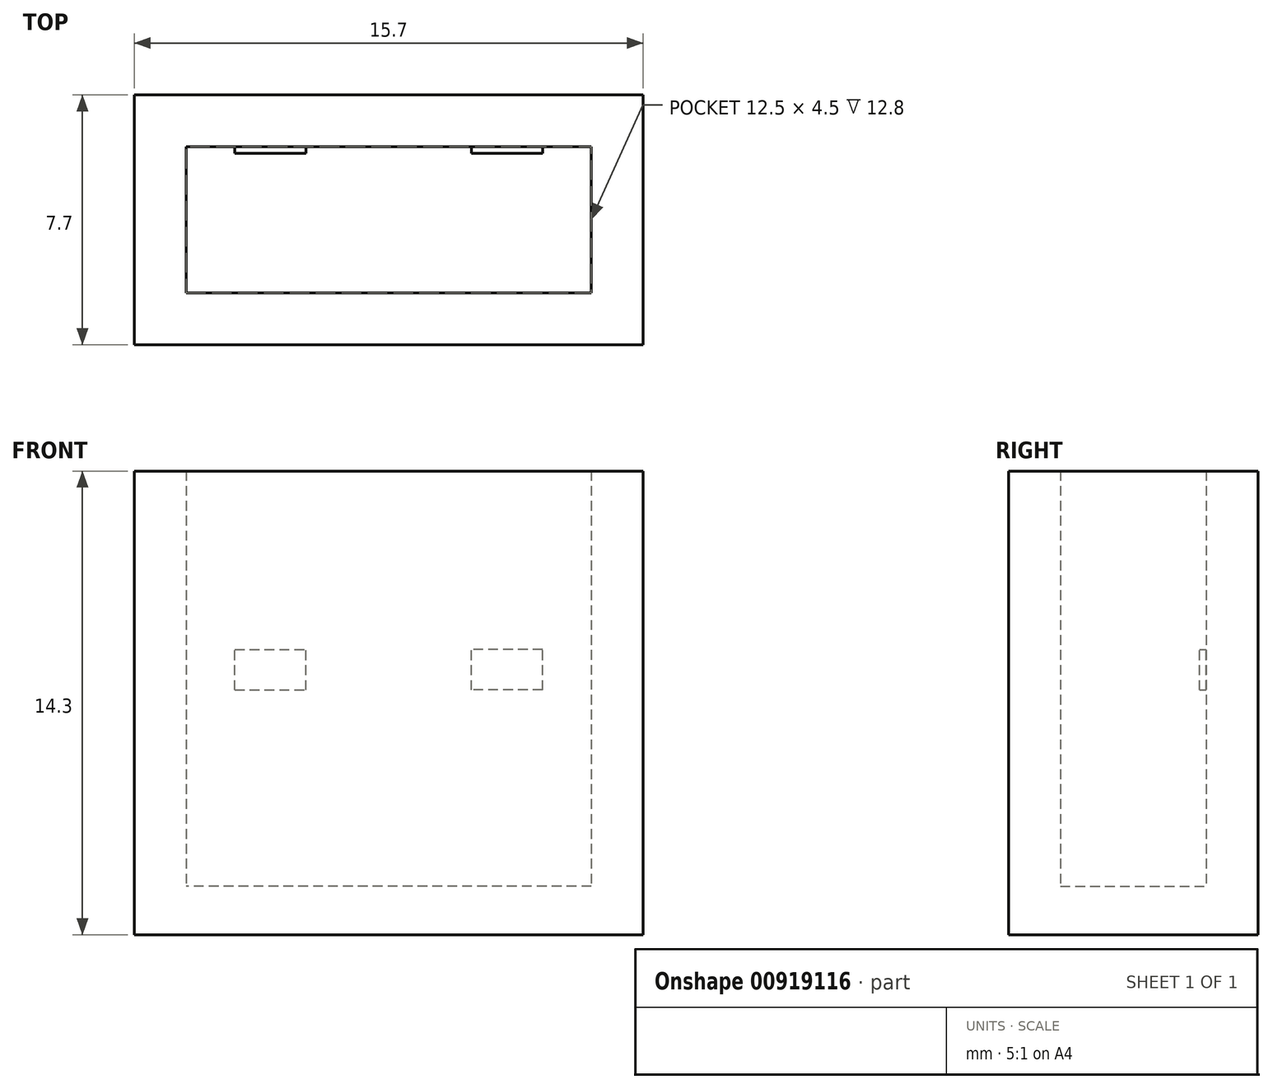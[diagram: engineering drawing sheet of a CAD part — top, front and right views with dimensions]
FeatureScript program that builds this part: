
annotation { "Feature Type Name" : "Feature", "Feature Type Description" : "" }
export const myFeature = defineFeature(function(context is Context, id is Id, definition is map)
    precondition{}
    {
        {
            var Q0;
            Q0=qCreatedBy(makeId("Top.planeOp"),FACE);
            var sketch = newSketch(context, id + "F0", { "sketchPlane" : qUnion([Q0])});
            skLineSegment(sketch, "E0.bottom", {"start": v(-6.25, 2.25) * mm, "end": v(6.25, 2.25) * mm});
            skLineSegment(sketch, "E0.top", {"start": v(-6.25, -2.25) * mm, "end": v(6.25, -2.25) * mm});
            skLineSegment(sketch, "E0.left", {"start": v(-6.25, 2.25) * mm, "end": v(-6.25, -2.25) * mm});
            skLineSegment(sketch, "E0.right", {"start": v(6.25, 2.25) * mm, "end": v(6.25, -2.25) * mm});
            skPoint(sketch, "E0.middle", {"position": v(0, 0) * mm});
            skLineSegment(sketch, "E1.0", {"start": v(-7.85, 3.85) * mm, "end": v(7.85, 3.85) * mm});
            skLineSegment(sketch, "E1.1", {"start": v(-7.85, 3.85) * mm, "end": v(-7.85, -3.85) * mm});
            skLineSegment(sketch, "E1.2", {"start": v(-7.85, -3.85) * mm, "end": v(7.85, -3.85) * mm});
            skLineSegment(sketch, "E1.3", {"start": v(7.85, 3.85) * mm, "end": v(7.85, -3.85) * mm});
            skSolve(sketch);
        }
        {
            var Q0;
            Q0 = qSketchRegion(id + "F0", true);
            var Q1;
            Q1=makeQuery(id+"F0.imprint","IMPRINT",FACE,{"disambiguationData":[TD([[makeQuery(id+"F0.imprint","IMPRINT",EDGE,{"derivedFrom":sQuery(id+"F0.wireOp",EDGE,"E0.bottom")}),-1.0]])]});
            extrude(context, id + "F1", {"entities" : qUnion([Q0, Q1]), "depth" : 1.5 * mm, "offsetDistance" : 25 * mm});
        }
        {
            var Q0;
            Q0=makeQuery(id+"F0.imprint","IMPRINT",FACE,{"disambiguationData":[TD([[makeQuery(id+"F0.imprint","IMPRINT",EDGE,{"derivedFrom":sQuery(id+"F0.wireOp",EDGE,"E0.bottom")}),1.0]])]});
            extrude(context, id + "F2", {"entities" : qUnion([Q0]), "operationType" : NewBodyOperationType.ADD, "depth" : 14.3 * mm, "offsetDistance" : 25 * mm});
        }
        {
            var Q0;
            Q0=makeQuery(id+"F2.opExtrude","SWEPT_FACE",FACE,{"disambiguationData":[OSD([sQuery(id+"F0.wireOp",EDGE,"E0.bottom")])]});
            var sketch = newSketch(context, id + "F3", { "sketchPlane" : qUnion([Q0])});
            skLineSegment(sketch, "E2.bottom", {"start": v(4.75, 7.55) * mm, "end": v(2.55, 7.55) * mm});
            skLineSegment(sketch, "E2.top", {"start": v(4.75, 8.8) * mm, "end": v(2.55, 8.8) * mm});
            skLineSegment(sketch, "E2.left", {"start": v(4.75, 7.55) * mm, "end": v(4.75, 8.8) * mm});
            skLineSegment(sketch, "E2.right", {"start": v(2.55, 7.55) * mm, "end": v(2.55, 8.8) * mm});
            skLineSegment(sketch, "E3.MirrorCS", {"start": v(-4.75, 8.8) * mm, "end": v(-2.55, 8.8) * mm});
            skLineSegment(sketch, "E4.MirrorCS", {"start": v(-2.55, 7.55) * mm, "end": v(-2.55, 8.8) * mm});
            skLineSegment(sketch, "E5.MirrorCS", {"start": v(-4.75, 7.55) * mm, "end": v(-2.55, 7.55) * mm});
            skLineSegment(sketch, "E6.MirrorCS", {"start": v(-4.75, 7.55) * mm, "end": v(-4.75, 8.8) * mm});
            skSolve(sketch);
        }
        {
            var Q0;
            Q0 = qSketchRegion(id + "F3", true);
            extrude(context, id + "F4", {"entities" : qUnion([Q0]), "operationType" : NewBodyOperationType.ADD, "depth" : 0.2 * mm, "offsetDistance" : 25 * mm});
        }
    });
